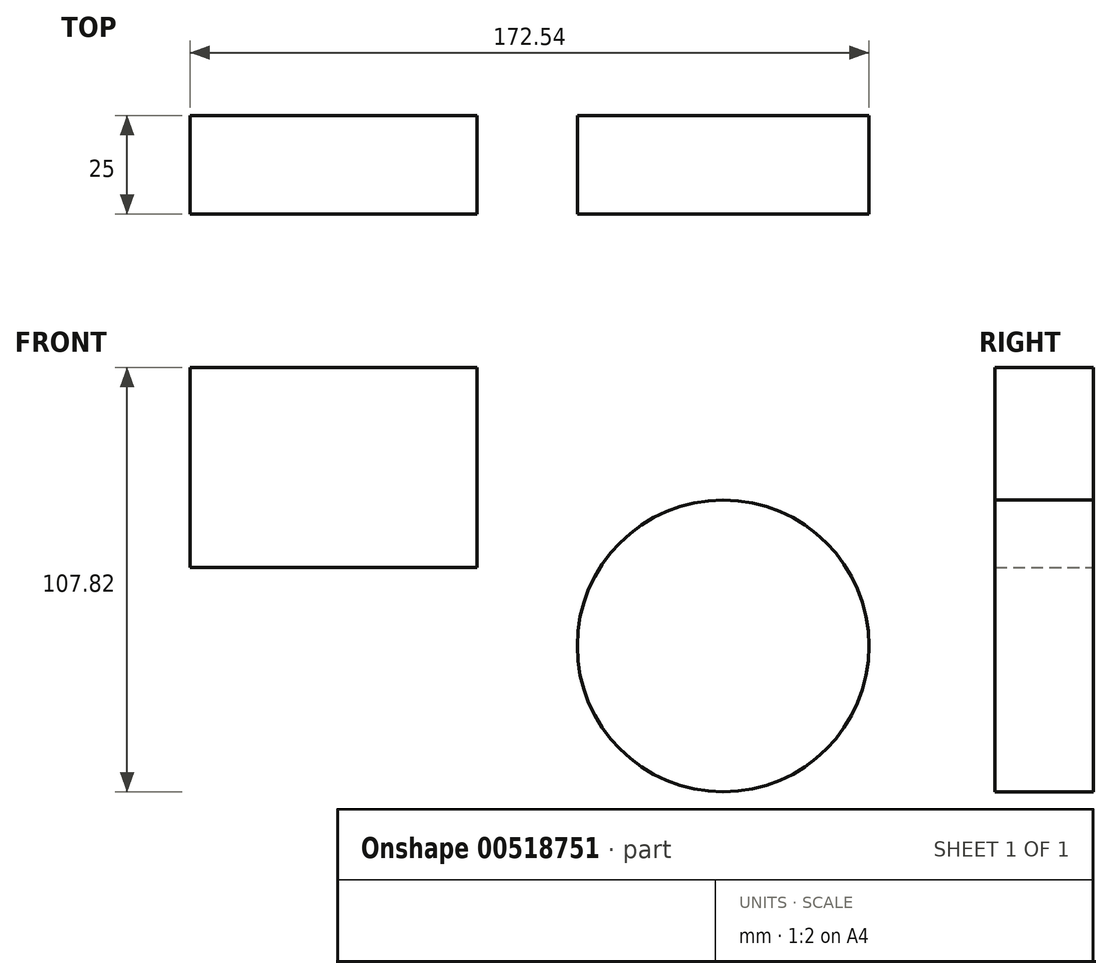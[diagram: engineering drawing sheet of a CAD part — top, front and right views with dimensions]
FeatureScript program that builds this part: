
annotation { "Feature Type Name" : "Feature", "Feature Type Description" : "" }
export const myFeature = defineFeature(function(context is Context, id is Id, definition is map)
    precondition{}
    {
        {
            var Q0;
            Q0=qCreatedBy(makeId("Front.planeOp"),FACE);
            var sketch = newSketch(context, id + "F0", { "sketchPlane" : qUnion([Q0])});
            skLineSegment(sketch, "E0.bottom", {"start": v(-105.01, 45.84) * mm, "end": v(-32.04, 45.84) * mm});
            skLineSegment(sketch, "E0.top", {"start": v(-105.01, -4.92) * mm, "end": v(-32.04, -4.92) * mm});
            skLineSegment(sketch, "E0.left", {"start": v(-105.01, 45.84) * mm, "end": v(-105.01, -4.92) * mm});
            skLineSegment(sketch, "E0.right", {"start": v(-32.04, 45.84) * mm, "end": v(-32.04, -4.92) * mm});
            skCircle(sketch, "E1", {"center": v(30.46, -24.9) * mm, "radius": 37.07 * mm});
            skSolve(sketch);
        }
        {
            var Q0;
            Q0 = qSketchRegion(id + "F0", true);
            extrude(context, id + "F1", {"entities" : qUnion([Q0]), "depth" : 25 * mm, "offsetDistance" : 25 * mm});
        }
    });
